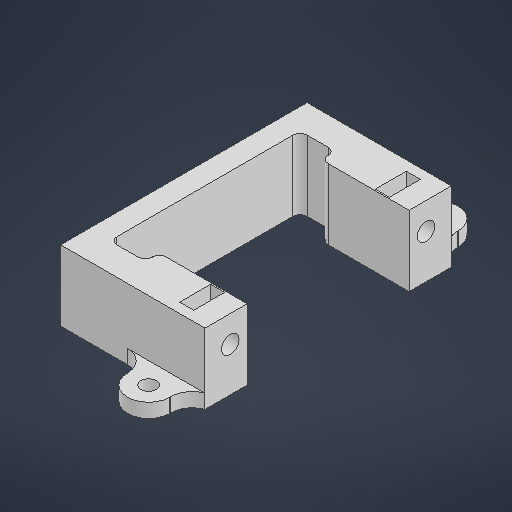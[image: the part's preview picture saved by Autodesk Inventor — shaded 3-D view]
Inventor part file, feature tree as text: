
AUTODESK INVENTOR PART (.ipt)
format: ipt  version: 2025.1 (Build 291241000, 241)  size: 578,048 bytes
history: native  units: mm
features: extrude x4, sketch x3, fillet x2
ambient origin geometry x8: Origin, YZ Plane, XZ Plane, XY Plane, X Axis, Y Axis, Z Axis, Center Point
bodies: Solid1 (feature_tree)
feature tree (9):
  sketch  "Sketch1"  dims[d0=23.0mm d1=17.5mm]
  extrude  "Extrusion1"  Depth=17.5mm
  extrude  "Extrusion2"  Depth=6.0mm
  extrude  "Extrusion3"  Depth=3.0mm
  extrude  "Extrusion4"  Depth=10.0mm TaperAngle=0.0deg
  fillet  "Fillet1"  Radius=4.4mm
  fillet  "Fillet2"  Radius=2.0mm
  sketch  "Sketch2"  dims[d2=3.0mm d4=6.0mm]
  sketch  "Sketch3"  dims[d5=10.0mm d6=0.0mm d7=2.5mm d9=10.0mm d10=0.0mm d11=4.4mm d13=2.0mm d14=7.0mm d15=0.0mm d16=2.2mm d17=2.2mm d18=3.0mm d19=3.0mm d21=2.0mm d22=0.0mm d23=3.0mm d24=41.0mm d26=5.0mm d27=5.0mm d28=2.0mm d29=1.0mm d31=27.8mm d33=6.2mm d34=3.0mm]
